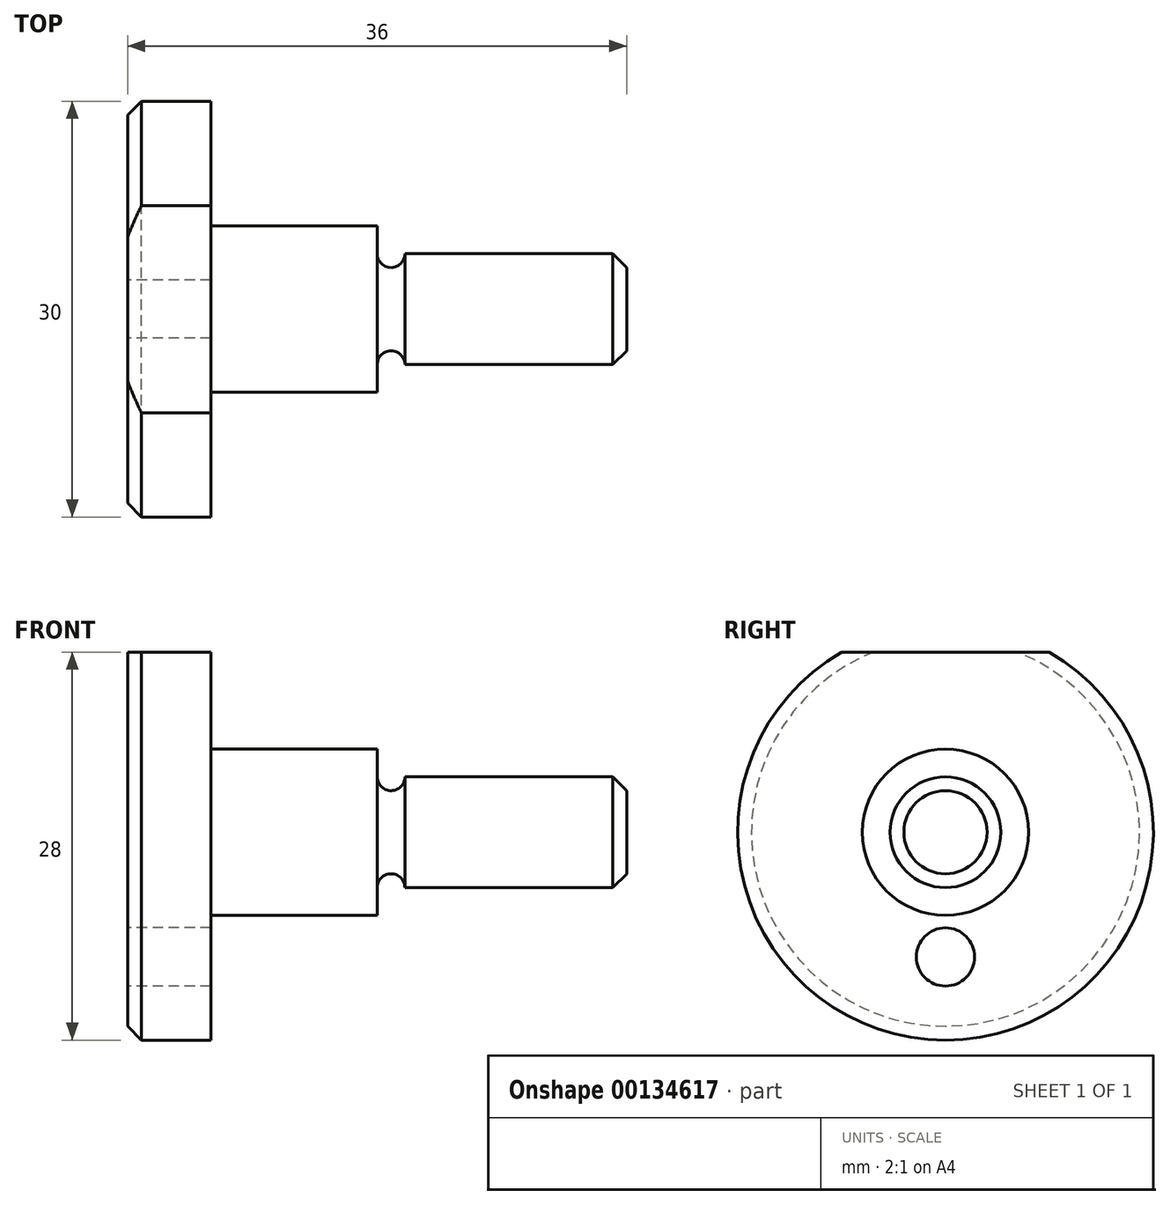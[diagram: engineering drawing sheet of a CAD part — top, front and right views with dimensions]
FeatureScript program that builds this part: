
annotation { "Feature Type Name" : "Feature", "Feature Type Description" : "" }
export const myFeature = defineFeature(function(context is Context, id is Id, definition is map)
    precondition{}
    {
        {
            var Q0;
            Q0=qCreatedBy(makeId("Top.planeOp"),FACE);
            var sketch = newSketch(context, id + "F0", { "sketchPlane" : qUnion([Q0])});
            skLineSegment(sketch, "E0", {"start": v(0, 0) * mm, "end": v(0, 15) * mm});
            skLineSegment(sketch, "E1", {"start": v(0, 15) * mm, "end": v(6, 15) * mm});
            skLineSegment(sketch, "E2", {"start": v(6, 15) * mm, "end": v(6, 6) * mm});
            skLineSegment(sketch, "E3", {"start": v(6, 6) * mm, "end": v(18, 6) * mm});
            skLineSegment(sketch, "E4", {"start": v(18, 6) * mm, "end": v(18, 4) * mm});
            skLineSegment(sketch, "E5", {"start": v(18, 3) * mm, "end": v(20, 3) * mm});
            skLineSegment(sketch, "E6", {"start": v(20, 4) * mm, "end": v(36, 4) * mm});
            skLineSegment(sketch, "E7", {"start": v(36, 4) * mm, "end": v(36, 0) * mm});
            skLineSegment(sketch, "E8", {"start": v(36, 0) * mm, "end": v(0, 0) * mm});
            skArc(sketch, "E9", {"start": v(18, 4) * mm, "mid": v(19, 3) * mm, "end": v(20, 4) * mm});
            skSolve(sketch);
        }
        {
            var Q0;
            Q0=makeQuery(id+"F0.imprint","IMPRINT",FACE,{"disambiguationData":[TD([[makeQuery(id+"F0.imprint","IMPRINT",EDGE,{"derivedFrom":sQuery(id+"F0.wireOp",EDGE,"E0")}),-1.0]])]});
            var Q1;
            Q1=sQuery(id+"F0.wireOp",EDGE,"E8");
            revolve(context, id + "F1", {"entities" : qUnion([Q0]), "axis" : qUnion([Q1]), "revolveType" : RevolveType.FULL});
        }
        {
            var Q0;
            Q0=makeQuery(id+"F1.opRevolve","SWEPT_FACE",FACE,{"disambiguationData":[OSD([sQuery(id+"F0.wireOp",EDGE,"E0")])]});
            var sketch = newSketch(context, id + "F2", { "sketchPlane" : qUnion([Q0])});
            skLineSegment(sketch, "E10.bottom", {"start": v(-25.44, 26.6) * mm, "end": v(23.42, 26.6) * mm});
            skLineSegment(sketch, "E10.top", {"start": v(-25.44, 13) * mm, "end": v(23.42, 13) * mm});
            skLineSegment(sketch, "E10.left", {"start": v(-25.44, 26.6) * mm, "end": v(-25.44, 13) * mm});
            skLineSegment(sketch, "E10.right", {"start": v(23.42, 26.6) * mm, "end": v(23.42, 13) * mm});
            skCircle(sketch, "E11.1", {"center": v(0, 0) * mm, "radius": 15 * mm});
            skSolve(sketch);
        }
        {
            var Q0;
            Q0=makeQuery(id+"F2.imprint","IMPRINT",FACE,{"disambiguationData":[TD([[makeQuery(id+"F2.imprint","IMPRINT",EDGE,{"derivedFrom":sQuery(id+"F2.wireOp",EDGE,"E10.bottom")}),-1.0]])]});
            var Q1;
            {var subQ0=sQuery(id+"F2.wireOp",EDGE,"E11.1");var subQ1=sQuery(id+"F2.wireOp",EDGE,"E10.top");var subQ2=makeQuery(id+"F2.imprint","INTERSECT",VERTEX,{"disambiguationData":[OD(0.0)],"derivedFrom":[subQ1,subQ0]});Q1=makeQuery(id+"F2.imprint","IMPRINT",FACE,{"disambiguationData":[TD([[makeQuery(id+"F2.imprint","IMPRINT",EDGE,{"disambiguationData":[TD([[subQ2,1.0]])],"derivedFrom":subQ0}),1.0]])]});}
            var Q2;
            {var subQ0=sQuery(id+"F2.wireOp",EDGE,"E10.top");var subQ1=sQuery(id+"F0.wireOp",EDGE,"E0");var subQ2=makeQuery(id+"F4OqCrwqI3KBJ6j_1.opChamfer","BLEND_EDGE",EDGE,{"blendedFrom":[makeQuery(id+"F1.opRevolve","SWEPT_EDGE",EDGE,{"disambiguationData":[OSD([subQ1,sQuery(id+"F0.wireOp",EDGE,"E1")])]}),makeQuery(id+"F1.opRevolve","SWEPT_FACE",FACE,{"disambiguationData":[OSD([subQ1])]})],"blendedInto":[makeQuery(id+"F1.opRevolve","SWEPT_FACE",FACE,{"disambiguationData":[OSD([subQ1])]})]});var subQ3=makeQuery(id+"F2.imprint","INTERSECT",VERTEX,{"disambiguationData":[OD(0.0)],"derivedFrom":[subQ2,subQ0]});Q2=makeQuery(id+"F2.imprint","IMPRINT",FACE,{"disambiguationData":[TD([[makeQuery(id+"F2.imprint","IMPRINT",EDGE,{"disambiguationData":[TD([[subQ3,-1.0]])],"derivedFrom":subQ0}),1.0]])]});}
            extrude(context, id + "F3", {"entities" : qUnion([Q0, Q1, Q2]), "operationType" : NewBodyOperationType.REMOVE, "oppositeDirection" : true, "depth" : 25 * mm});
        }
        {
            var Q0;
            Q0=makeQuery(id+"F1.opRevolve","SWEPT_EDGE",EDGE,{"disambiguationData":[OSD([sQuery(id+"F0.wireOp",EDGE,"E0"),sQuery(id+"F0.wireOp",EDGE,"E1")])]});
            var Q1;
            Q1=makeQuery(id+"F3.boolean.opBoolean","COPY",EDGE,{"derivedFrom":makeQuery(id+"F3.opExtrude","CAP_EDGE",EDGE,{"disambiguationData":[OSD([sQuery(id+"F2.wireOp",EDGE,"E10.top")])],"isStart":true})});
            var Q2;
            Q2=makeQuery(id+"F1.opRevolve","SWEPT_EDGE",EDGE,{"disambiguationData":[OSD([sQuery(id+"F0.wireOp",EDGE,"E6"),sQuery(id+"F0.wireOp",EDGE,"E7")])]});
            chamfer(context, id + "F4", {"entities" : qUnion([Q0, Q1, Q2]), "width" : 1 * mm, "tangentPropagation" : true});
        }
        {
            var Q0;
            Q0=makeQuery(id+"F1.opRevolve","SWEPT_FACE",FACE,{"disambiguationData":[OSD([sQuery(id+"F0.wireOp",EDGE,"E0")])]});
            var sketch = newSketch(context, id + "F5", { "sketchPlane" : qUnion([Q0])});
            skCircle(sketch, "E12", {"center": v(0, -9) * mm, "radius": 2.1 * mm});
            skSolve(sketch);
        }
        {
            var Q0;
            Q0=makeQuery(id+"F5.imprint","IMPRINT",FACE,{"disambiguationData":[TD([[makeQuery(id+"F5.imprint","IMPRINT",EDGE,{"derivedFrom":sQuery(id+"F5.wireOp",EDGE,"E12")}),1.0]])]});
            extrude(context, id + "F6", {"entities" : qUnion([Q0]), "operationType" : NewBodyOperationType.REMOVE, "oppositeDirection" : true, "depth" : 6 * mm});
        }
    });
